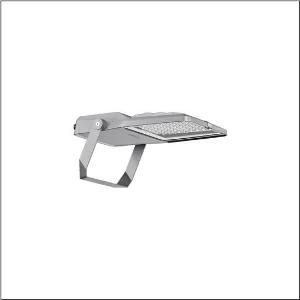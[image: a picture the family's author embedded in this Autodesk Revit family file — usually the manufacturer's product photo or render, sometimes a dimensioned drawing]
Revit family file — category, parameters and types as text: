
# Revit family: floodlight_fl_21_iq_mini___pl64_5xa7772c4e1a_6403
name_source: partatom
category: Lighting Fixtures
units: mm (PartAtom-declared; Revit-internal decimal feet)

## family parameters
Cut with Voids When Loaded = No
Host = Face
Light Source = No
Part Type = Normal
Room Calculation Point = No
Round Connector Dimension = Use Diameter
Shared = No

## types (1)
- --- (1 x LED, 12280 lm, 87.2 W, 4000K)
    Apparent Load = 87 VA
    CIE Flux Codes = 28 80 98 100 100
    Color Rendering = 70
    Color Temperature = 4000K
    Default Elevation = 1800 mm
    Description = Floodlight FL 21 iQ mini, floodlight, primary light control with lens, of PMMA, primary optical cover: protective disc, of toughened safety glass, transparent, light distribution: PL64, light emission: direct distribution, installation type: surface-mounted, LED, High Power LED, rated luminous flux: 12.280lm, luminous efficacy: 141lm/W, light colour: 740, colour temperature: 4000K, control: Street-Remote, Auto-Match, Temp-Guard, Night-Set, Smart-Wire, Desk-Remote (wireless, voltage-free reading and setting of iQ features in the workshop via application-optimized NFC function/RFID function), optimised constant luminous flux control (CLO 2.0), with terminal, 6-pole, mains connection: 220..240V, AC, 50/60Hz, start of lifetime: 87W, end of service life: 92W, reduction: 40W, luminaire housing, of diecast aluminium, powder-coated, Siteco® metallic grey (DB 702S), corrosivity category C5 mid according to DIN EN ISO 12944, sealing non-destructively replaceable, mounting bracket, of steel, galvanised, powder-coated, Siteco® metallic grey (DB 702S), protection rating (complete): IP66, insulation class (complete): insulation class II (safety insulation), certification: CE, ENEC, VDE, protection symbol: D, impact resistance: IK08, permissible operating ambient temperature: -40..+40°C, permissible operating ambient temperature for outdoor applications: -40..+50°C, standard: DIN EN 12944, LABS conformity tested according to VDMA 24364:2018-05, packaging unit: 1 piece

Light Distribution: PL64
    Height = 70 mm
    Lamp = 1 x LED
    Lamp Light Flux = 12280 lm
    Lamp Power = 87.2 W
    Lamp count = 1
    Length = 485 mm
    Luminous efficacy = 141 lm/W
    Manufacturer = Siteco
    ModVariant = No
    Model = 5XA7772C4E1A
    Number of Poles = 1
    OnlyDefault = Yes
    Power Factor = 1
    Product Name = Floodlight FL 21 iQ mini | PL64
    Product group = floodlight | pylon annexe
    ProductGroupID = 6200
    Protection Class = Protection class II
    Protection Degree = IP 66
    RLX_Detail_Level = 1
    RLX_Emergency_Light_Flux = 0 lm
    RLX_Emergency_Type = 0
    RLX_Emergency_Type_DB = No
    RlxData = <blob elided: 96241 chars, md5=cfbd8fe3>
    Socket = socket
    Standby Power = 0 W
    System Light Flux = 12280 lm
    System Power = 87 W
    Type Comments = factory setting: luminous flux: 100 % | dim-lin: 254 | 456 mA
    Type Image = l_1006845.jpg
    URL = http://relux.com
    VarID = @adj_098589
    Voltage = 0 V
    Weight = 0.00 kg
    Width = 337 mm

## geometry (parser evidence)
native form markers: Blend x4, Sweep x11
no freeform markers — native parametric forms only
